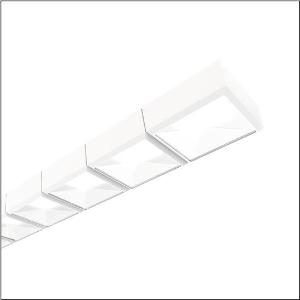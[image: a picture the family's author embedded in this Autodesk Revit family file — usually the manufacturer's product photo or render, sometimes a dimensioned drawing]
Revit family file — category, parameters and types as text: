
# Revit family: scriptus_11_5mz313d04wa
name_source: partatom
category: Lighting Fixtures
units: mm (PartAtom-declared; Revit-internal decimal feet)

## family parameters
Cut with Voids When Loaded = No
Host = Face
Light Source = No
Part Type = Normal
Room Calculation Point = No
Round Connector Dimension = Use Diameter
Shared = No

## types (1)
- Scriptus 11 (1 x LED 4000K / CRI = 80 (unbekannt), 2660 lm / 4010 lm, 4000K)
    Apparent Load = 99 VA
    CIE Flux Codes = - - - 0 100 / 82 95 99 100 100
    Color Rendering = 80
    Color Temperature = 4000K
    Default Elevation = 1800 mm
    Description = Scriptus 11, office luminaire, primary optical cover: lenses, CAT 2 (L<= 3000cd/m²), light emission: direct/indirect distribution, primary light characteristic: symmetric, installation type: suspended mounting, LED, rated luminous flux: 13.330lm, luminous efficacy: 134lm/W, light colour: 840, colour temperature: 4000K, control gear: DALI, with terminal, 5-pole, mains connection: 230V, AC, 50Hz, rated input power: 99W, LED, control gear: ECG DALI, housing, luminaire housing, of aluminium, traffic white (RAL 9016), length: 2.648mm, width: 114mm, height: 57mm, protection rating (complete): IP20, insulation class (complete): insulation class I (protective earthing), certification: CE, ENEC, VDE, protection symbol: F, permissible operating ambient temperature: 0..+35°C, standard: EN 50419, packaging unit: 1 piece
    Height = 57 mm
    Lamp = 1 x LED 4000K / CRI >= 80 (unbekannt)
    Lamp Light Flux = 2660 lm / 4010 lm
    Lamp count = 1
    Length = 2648 mm
    Luminous efficacy = 134 lm/W
    Manufacturer = Siteco
    ModVariant = No
    Model = 5MZ313D04WA
    Mounting Place = Ceiling
    Mounting Type = Pendant
    Number of Poles = 1
    OnlyDefault = Yes
    Power Factor = 1
    Product Name = Scriptus 11
    Product group = office luminaire | ceiling pendant
    ProductGroupID = 903
    Protection Class = Protection class I
    Protection Degree = IP 20
    RLX_Detail_Level = 1
    RLX_Emergency_Light_Flux = 0 lm
    RLX_Emergency_Type = 0
    RLX_Emergency_Type_DB = No
    RlxData = <blob elided: 31653 chars, md5=9cbdce42>
    Socket = socket
    Standby Power = 0 W
    System Light Flux = 13340 lm
    System Power = 99 W
    Type Comments = Product without accessories
    Type Image = l_1004839.jpg
    URL = http://relux.com
    VarID = ---
    Voltage = 0 V
    Weight = 0.00 kg
    Width = 114 mm

## geometry (parser evidence)
native form markers: Blend x4, Sweep x22
no freeform markers — native parametric forms only
